# Revit family: Zumtobel SUI TG6
name_source: partatom
category: Lighting Fixtures
revit_build: Autodesk Revit 2018 (Build: 20170223_1515(x64)
units: mm (PartAtom-declared; Revit-internal decimal feet)

## family parameters
Cut with Voids When Loaded = No
Host = Face
Light Source = Yes
OmniClass Number = 23.80.70.11
OmniClass Title = Luminaries for Internal Lighting
Part Type = Normal
Room Calculation Point = No
Round Connector Dimension = Use Diameter
Shared = No

## types (4) — shared parameters
Assembly Code = D5020200
Color Filter = 16777215
Description = LED luminaire
Dimming Lamp Color Temperature Shift = <None>
Height = 79 mm
Lamp = LED
Length = 398 mm  [stored 1.30577 ft]
Manufacturer = Zumtobel Lighting
Tilt Angle = -90.00°
URL = http://www.zumtobel.com
Voltage = 230 V
Width = 35 mm  [stored 0.114829 ft]
zero-valued in all types: Default Elevation

## per-type parameters (varying)
| type | Apparent Load | Model | Photometric Web File |
| SUI TSG6 1700-930 LDO 3CY FL BK BK | 21 VA | 60211090 | 60211090_(STD_LEO).IES |
| SUI TG6 1000-940 LDO 3CY WWB BK WH | 21 VA | 60211067 | 60211067_(STD_LEO).IES |
| SUI TSG6 1700-930 SWI 3CV FL BK WH | 21 VA | 60211039 | 60211039_(STD_LEO).IES |
| SUI TG6 2000-930 SWI 3CV FL BK WH | 25 VA | 60211029 | 60211029_(STD_LEO).IES |

note: [stored X ft] marks values corroborated as IEEE doubles in the binary element streams (Revit-internal decimal feet)

## geometry (parser evidence)
native form markers: Sweep x7
no freeform markers — native parametric forms only
